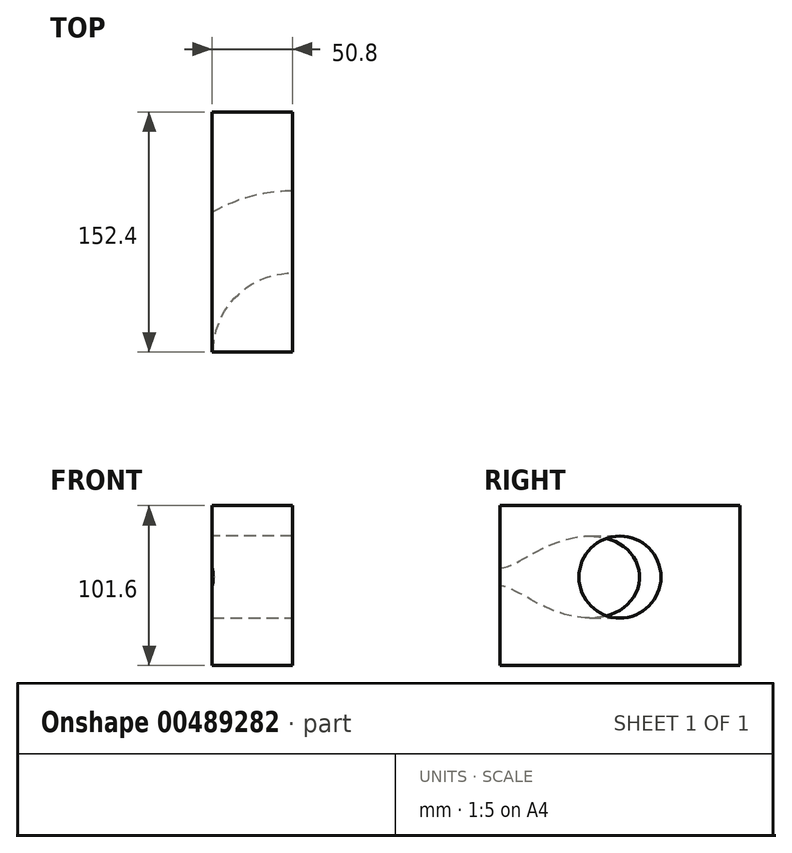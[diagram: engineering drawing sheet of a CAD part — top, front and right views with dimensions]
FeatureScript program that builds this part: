
annotation { "Feature Type Name" : "Feature", "Feature Type Description" : "" }
export const myFeature = defineFeature(function(context is Context, id is Id, definition is map)
    precondition{}
    {
        {
            var Q0;
            Q0=qCreatedBy(makeId("Front.planeOp"),FACE);
            var sketch = newSketch(context, id + "F0", { "sketchPlane" : qUnion([Q0])});
            skLineSegment(sketch, "E0.bottom", {"start": v(23.6, 43) * mm, "end": v(74.4, 43) * mm});
            skLineSegment(sketch, "E0.top", {"start": v(23.6, 144.6) * mm, "end": v(74.4, 144.6) * mm});
            skLineSegment(sketch, "E0.left", {"start": v(23.6, 43) * mm, "end": v(23.6, 144.6) * mm});
            skLineSegment(sketch, "E0.right", {"start": v(74.4, 43) * mm, "end": v(74.4, 144.6) * mm});
            skSolve(sketch);
        }
        {
            var Q0;
            Q0=makeQuery(id+"F0.imprint","IMPRINT",FACE,{"disambiguationData":[TD([[makeQuery(id+"F0.imprint","IMPRINT",EDGE,{"derivedFrom":sQuery(id+"F0.wireOp",EDGE,"E0.bottom")}),1.0]])]});
            extrude(context, id + "F1", {"entities" : qUnion([Q0]), "endBound" : BoundingType.SYMMETRIC, "depth" : 152.4 * mm, "hasDraft" : true, "draftAngle" : 0 * degree});
        }
        {
            var Q0;
            {var subQ0=makeQuery(id+"F1.opExtrude","SWEPT_FACE",FACE,{"disambiguationData":[OSD([sQuery(id+"F0.wireOp",EDGE,"E0.right")])]});Q0=makeQuery(id+"F1.*.booleanUnion.opBoolean","MERGE",FACE,{"derivedFrom":[makeQuery(id+"F1.*.split.splitOp","SPLIT",FACE,{"derivedFrom":subQ0}),makeQuery(id+"F1.*.split.splitOp","SPLIT",FACE,{"derivedFrom":subQ0,"isFromBackBody":true})]});}
            var sketch = newSketch(context, id + "F2", { "sketchPlane" : qUnion([Q0])});
            skCircle(sketch, "E1", {"center": v(0, 99.16) * mm, "radius": 26.04 * mm});
            skSolve(sketch);
        }
        {
            var Q0;
            Q0=makeQuery(id+"F2.imprint","IMPRINT",FACE,{"disambiguationData":[TD([[makeQuery(id+"F2.imprint","IMPRINT",EDGE,{"derivedFrom":sQuery(id+"F2.wireOp",EDGE,"E1")}),1.0]])]});
            var Q1;
            Q1=makeQuery(id+"F1.opExtrude","CAP_EDGE",EDGE,{"disambiguationData":[OSD([sQuery(id+"F0.wireOp",EDGE,"E0.right")])],"isStart":false});
            revolve(context, id + "F3", {"operationType" : NewBodyOperationType.REMOVE, "entities" : qUnion([Q0]), "axis" : qUnion([Q1]), "revolveType" : RevolveType.FULL, "oppositeDirection" : true});
        }
    });
